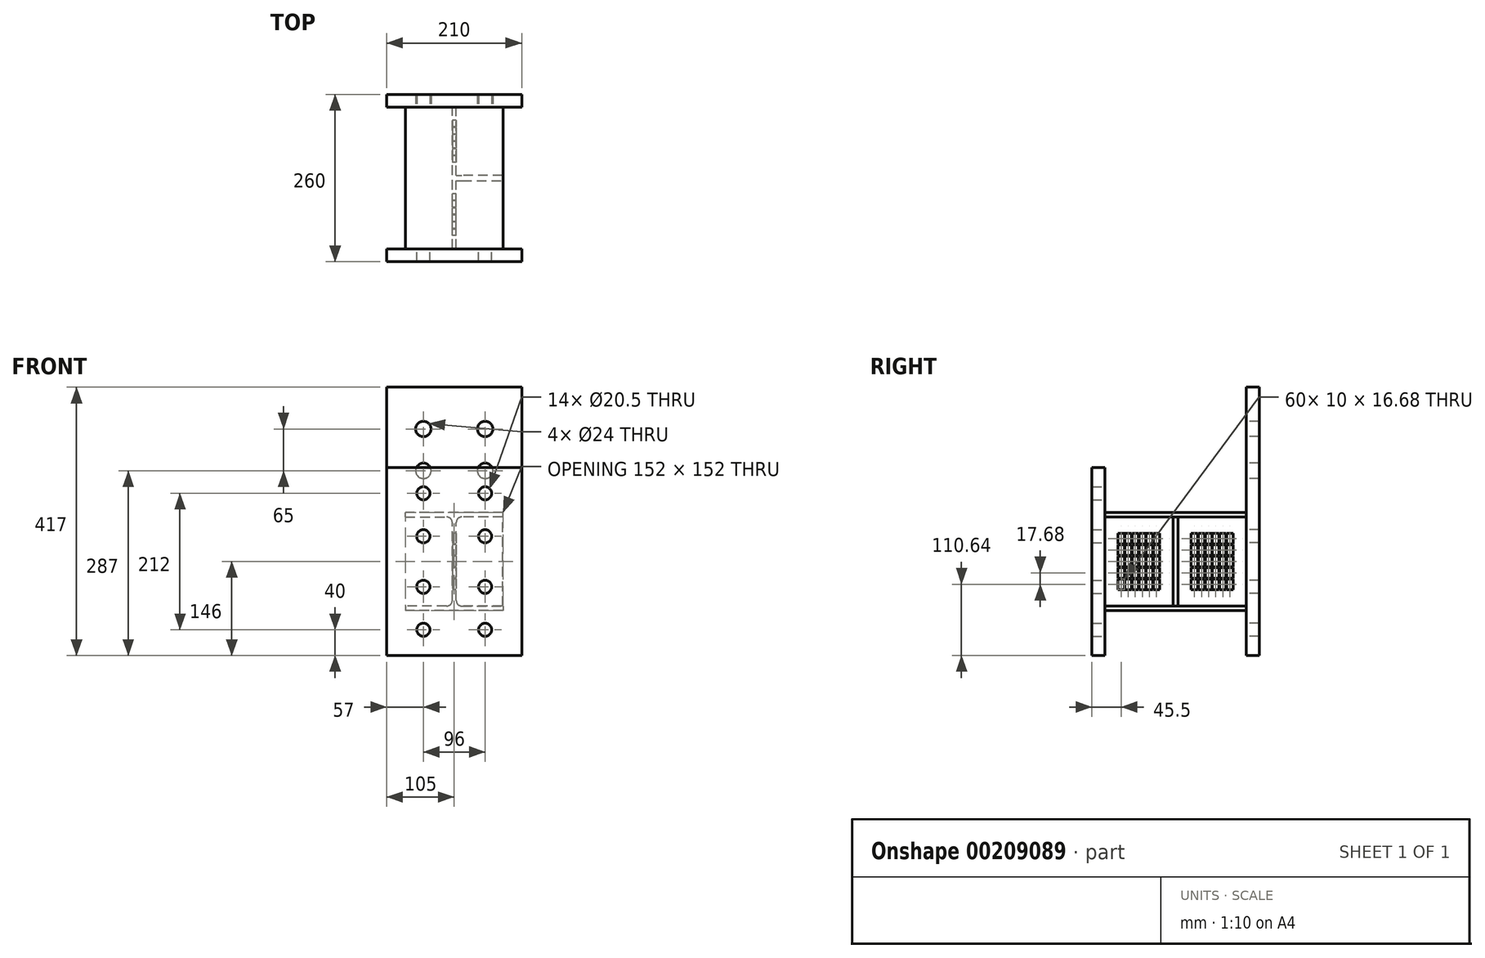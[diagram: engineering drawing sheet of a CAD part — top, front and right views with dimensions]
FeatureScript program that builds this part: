
annotation { "Feature Type Name" : "Feature", "Feature Type Description" : "" }
export const myFeature = defineFeature(function(context is Context, id is Id, definition is map)
    precondition{}
    {
        {
            var Q0;
            Q0=qCreatedBy(makeId("Front.planeOp"),FACE);
            var sketch = newSketch(context, id + "F0", { "sketchPlane" : qUnion([Q0])});
            skLineSegment(sketch, "E0.left", {"start": v(3.05, -60.3) * mm, "end": v(3.05, 60.3) * mm});
            skLineSegment(sketch, "E0.right", {"start": v(-3.05, -60.3) * mm, "end": v(-3.05, 60.3) * mm});
            skPoint(sketch, "E0.middle", {"position": v(0, 0) * mm});
            skLineSegment(sketch, "E1.bottom", {"start": v(76, 69.2) * mm, "end": v(11.95, 69.2) * mm});
            skLineSegment(sketch, "E1.top", {"start": v(76, 76) * mm, "end": v(-76, 76) * mm});
            skLineSegment(sketch, "E1.left", {"start": v(76, 69.2) * mm, "end": v(76, 76) * mm});
            skLineSegment(sketch, "E1.right", {"start": v(-76, 69.2) * mm, "end": v(-76, 76) * mm});
            skLineSegment(sketch, "E2.bottom", {"start": v(-11.95, -69.2) * mm, "end": v(-76, -69.2) * mm});
            skLineSegment(sketch, "E2.top", {"start": v(76, -76) * mm, "end": v(-76, -76) * mm});
            skLineSegment(sketch, "E2.left", {"start": v(76, -69.2) * mm, "end": v(76, -76) * mm});
            skLineSegment(sketch, "E2.right", {"start": v(-76, -69.2) * mm, "end": v(-76, -76) * mm});
            skPoint(sketch, "E3.newPointB", {"position": v(-76, 69.2) * mm});
            skArc(sketch, "E3.filletArc", {"start": v(11.95, 69.2) * mm, "mid": v(5.66, 66.6) * mm, "end": v(3.05, 60.3) * mm});
            skLineSegment(sketch, "E4", {"start": v(-76, 69.2) * mm, "end": v(-11.95, 69.2) * mm});
            skArc(sketch, "E5.filletArc", {"start": v(-3.05, 60.3) * mm, "mid": v(-5.66, 66.6) * mm, "end": v(-11.95, 69.2) * mm});
            skPoint(sketch, "E6.newPointA", {"position": v(76, -69.2) * mm});
            skArc(sketch, "E6.filletArc", {"start": v(-11.95, -69.2) * mm, "mid": v(-5.66, -66.6) * mm, "end": v(-3.05, -60.3) * mm});
            skLineSegment(sketch, "E7", {"start": v(11.95, -69.2) * mm, "end": v(76, -69.2) * mm});
            skArc(sketch, "E8.filletArc", {"start": v(3.05, -60.3) * mm, "mid": v(5.66, -66.6) * mm, "end": v(11.95, -69.2) * mm});
            skSolve(sketch);
        }
        {
            var Q0;
            Q0=qSketchRegion(id+"F0",true);
            extrude(context, id + "F1", {"entities" : qUnion([Q0]), "depth" : 220 * mm, "symmetric" : true});
        }
        {
            var Q0;
            Q0=makeQuery(id+"F1.opExtrude","SWEPT_FACE",FACE,{"disambiguationData":[OSD([sQuery(id+"F0.wireOp",EDGE,"E0.left")])]});
            var sketch = newSketch(context, id + "F2", { "sketchPlane" : qUnion([Q0])});
            skLineSegment(sketch, "E9.bottom", {"start": v(4, -69.2) * mm, "end": v(-4, -69.2) * mm});
            skLineSegment(sketch, "E9.top", {"start": v(4, 69.2) * mm, "end": v(-4, 69.2) * mm});
            skLineSegment(sketch, "E9.left", {"start": v(4, -69.2) * mm, "end": v(4, 69.2) * mm});
            skLineSegment(sketch, "E9.right", {"start": v(-4, -69.2) * mm, "end": v(-4, 69.2) * mm});
            skPoint(sketch, "E9.middle", {"position": v(0, 0) * mm});
            skSolve(sketch);
        }
        {
            var Q0;
            Q0=qSketchRegion(id+"F2",true);
            extrude(context, id + "F3", {"entities" : qUnion([Q0]), "operationType" : NewBodyOperationType.ADD, "depth" : 72 * mm});
        }
        {
            var Q0;
            Q0=makeQuery(id+"F1.opExtrude","CAP_FACE",FACE,{"disambiguationData":[OSD([sQuery(id+"F0.wireOp",EDGE,"E0.left"),sQuery(id+"F0.wireOp",EDGE,"E0.right"),sQuery(id+"F0.wireOp",EDGE,"E1.bottom"),sQuery(id+"F0.wireOp",EDGE,"E1.top"),sQuery(id+"F0.wireOp",EDGE,"E1.left"),sQuery(id+"F0.wireOp",EDGE,"E1.right"),sQuery(id+"F0.wireOp",EDGE,"E2.bottom"),sQuery(id+"F0.wireOp",EDGE,"E2.top"),sQuery(id+"F0.wireOp",EDGE,"E2.left"),sQuery(id+"F0.wireOp",EDGE,"E2.right"),sQuery(id+"F0.wireOp",EDGE,"E3.filletArc"),sQuery(id+"F0.wireOp",EDGE,"E4"),sQuery(id+"F0.wireOp",EDGE,"E5.filletArc"),sQuery(id+"F0.wireOp",EDGE,"E6.filletArc"),sQuery(id+"F0.wireOp",EDGE,"E7"),sQuery(id+"F0.wireOp",EDGE,"E8.filletArc")])],"isStart":false});
            var sketch = newSketch(context, id + "F4", { "sketchPlane" : qUnion([Q0])});
            skLineSegment(sketch, "E10.bottom", {"start": v(105, -146) * mm, "end": v(-105, -146) * mm});
            skLineSegment(sketch, "E10.top", {"start": v(105, 146) * mm, "end": v(-105, 146) * mm});
            skLineSegment(sketch, "E10.left", {"start": v(105, -146) * mm, "end": v(105, 146) * mm});
            skLineSegment(sketch, "E10.right", {"start": v(-105, -146) * mm, "end": v(-105, 146) * mm});
            skPoint(sketch, "E10.middle", {"position": v(0, 0) * mm});
            skCircle(sketch, "E11", {"center": v(-48, 106) * mm, "radius": 10.25 * mm});
            skCircle(sketch, "E12", {"center": v(-48, 39.2) * mm, "radius": 10.25 * mm});
            skCircle(sketch, "E13", {"center": v(-48, -39.2) * mm, "radius": 10.25 * mm});
            skCircle(sketch, "E14", {"center": v(-48, -106) * mm, "radius": 10.25 * mm});
            skCircle(sketch, "E15.MirrorC", {"center": v(48, -39.2) * mm, "radius": 10.25 * mm});
            skCircle(sketch, "E16.MirrorC", {"center": v(48, 39.2) * mm, "radius": 10.25 * mm});
            skCircle(sketch, "E17.MirrorC", {"center": v(48, -106) * mm, "radius": 10.25 * mm});
            skCircle(sketch, "E18.MirrorC", {"center": v(48, 106) * mm, "radius": 10.25 * mm});
            skSolve(sketch);
        }
        {
            var Q0;
            Q0=qSketchRegion(id+"F4",true);
            extrude(context, id + "F5", {"entities" : qUnion([Q0]), "operationType" : NewBodyOperationType.ADD, "depth" : 20 * mm});
        }
        {
            var Q0;
            Q0=makeQuery(id+"F1.opExtrude","CAP_FACE",FACE,{"disambiguationData":[OSD([sQuery(id+"F0.wireOp",EDGE,"E0.left"),sQuery(id+"F0.wireOp",EDGE,"E0.right"),sQuery(id+"F0.wireOp",EDGE,"E1.bottom"),sQuery(id+"F0.wireOp",EDGE,"E1.top"),sQuery(id+"F0.wireOp",EDGE,"E1.left"),sQuery(id+"F0.wireOp",EDGE,"E1.right"),sQuery(id+"F0.wireOp",EDGE,"E2.bottom"),sQuery(id+"F0.wireOp",EDGE,"E2.top"),sQuery(id+"F0.wireOp",EDGE,"E2.left"),sQuery(id+"F0.wireOp",EDGE,"E2.right"),sQuery(id+"F0.wireOp",EDGE,"E3.filletArc"),sQuery(id+"F0.wireOp",EDGE,"E4"),sQuery(id+"F0.wireOp",EDGE,"E5.filletArc"),sQuery(id+"F0.wireOp",EDGE,"E6.filletArc"),sQuery(id+"F0.wireOp",EDGE,"E7"),sQuery(id+"F0.wireOp",EDGE,"E8.filletArc")])],"isStart":true});
            var sketch = newSketch(context, id + "F6", { "sketchPlane" : qUnion([Q0])});
            skLineSegment(sketch, "E19.bottom", {"start": v(-105, -146) * mm, "end": v(105, -146) * mm});
            skLineSegment(sketch, "E19.top", {"start": v(-105, 271) * mm, "end": v(105, 271) * mm});
            skLineSegment(sketch, "E19.left", {"start": v(-105, -146) * mm, "end": v(-105, 271) * mm});
            skLineSegment(sketch, "E19.right", {"start": v(105, 271) * mm, "end": v(105, -146) * mm});
            skCircle(sketch, "E20", {"center": v(-48, 39.2) * mm, "radius": 10.25 * mm});
            skCircle(sketch, "E21.MirrorC", {"center": v(-48, -106) * mm, "radius": 10.25 * mm});
            skCircle(sketch, "E22.MirrorC", {"center": v(-48, -39.2) * mm, "radius": 10.25 * mm});
            skLineSegment(sketch, "E23", {"start": v(0, 0) * mm, "end": v(0, 68.37) * mm});
            skPoint(sketch, "E23.endSnap0", {"position": v(0, 76) * mm});
            skCircle(sketch, "E24.MirrorC", {"center": v(48, -106) * mm, "radius": 10.25 * mm});
            skCircle(sketch, "E25.MirrorC", {"center": v(48, -39.2) * mm, "radius": 10.25 * mm});
            skCircle(sketch, "E26.MirrorC", {"center": v(48, 39.2) * mm, "radius": 10.25 * mm});
            skCircle(sketch, "E27", {"center": v(-48, 141) * mm, "radius": 12 * mm});
            skCircle(sketch, "E28", {"center": v(-48, 206) * mm, "radius": 12 * mm});
            skCircle(sketch, "E29.MirrorC", {"center": v(48, 141) * mm, "radius": 12 * mm});
            skCircle(sketch, "E30.MirrorC", {"center": v(48, 206) * mm, "radius": 12 * mm});
            skSolve(sketch);
        }
        {
            var Q0;
            Q0=qSketchRegion(id+"F6",true);
            extrude(context, id + "F7", {"entities" : qUnion([Q0]), "operationType" : NewBodyOperationType.ADD, "depth" : 20 * mm});
        }
        {
            var Q0;
            {var subQ2=sQuery(id+"F0.wireOp",EDGE,"E0.right");Q0=makeQuery(id+"F3.boolean.opBoolean","SPLIT",FACE,{"disambiguationData":[TD([makeQuery(id+"F3.opExtrude","SWEPT_FACE",FACE,{"disambiguationData":[OSD([sQuery(id+"F2.wireOp",EDGE,"E9.left")])]})])],"derivedFrom":makeQuery(id+"F1.opExtrude","SWEPT_FACE",FACE,{"disambiguationData":[OSD([subQ2])]})});}
            var sketch = newSketch(context, id + "F8", { "sketchPlane" : qUnion([Q0])});
            skPoint(sketch, "E31.middle", {"position": v(0, 0) * mm});
            skPoint(sketch, "E31.middle.positionSnap0", {"position": v(53, 0) * mm});
            skPoint(sketch, "E31.middle.positionSnap1", {"position": v(0, 60.3) * mm});
            skPoint(sketch, "E31.centerSnap0", {"position": v(53, 0) * mm});
            skPoint(sketch, "E31.centerSnap1", {"position": v(0, 60.3) * mm});
            skPoint(sketch, "E32.MirrorP", {"position": v(-35, 0) * mm});
            skPoint(sketch, "E33.middle", {"position": v(-57, 26.52) * mm});
            skPoint(sketch, "E34.middle", {"position": v(-57, 8.84) * mm});
            skPoint(sketch, "E35.middle", {"position": v(-57, -8.84) * mm});
            skPoint(sketch, "E36.middle", {"position": v(-57, -26.52) * mm});
            skPoint(sketch, "E37.middle", {"position": v(-57, -44.2) * mm});
            skPoint(sketch, "E38.middle", {"position": v(-57, 44.2) * mm});
            skPoint(sketch, "E39.middle", {"position": v(-90, 0) * mm});
            skPoint(sketch, "E40.middle", {"position": v(-79, 0) * mm});
            skPoint(sketch, "E41.middle", {"position": v(-68, 0) * mm});
            skPoint(sketch, "E42.middle", {"position": v(-46, 0) * mm});
            skPoint(sketch, "E43.middle", {"position": v(-24, 0) * mm});
            skLineSegment(sketch, "E44.bottom", {"start": v(-89.5, 43.7) * mm, "end": v(-79.5, 43.7) * mm});
            skLineSegment(sketch, "E44.top", {"start": v(-89.5, 27.02) * mm, "end": v(-79.5, 27.02) * mm});
            skLineSegment(sketch, "E44.left", {"start": v(-89.5, 43.7) * mm, "end": v(-89.5, 27.02) * mm});
            skLineSegment(sketch, "E44.right", {"start": v(-79.5, 43.7) * mm, "end": v(-79.5, 27.02) * mm});
            skLineSegment(sketch, "E45.bottom", {"start": v(-78.5, 43.7) * mm, "end": v(-68.5, 43.7) * mm});
            skLineSegment(sketch, "E45.top", {"start": v(-78.5, 27.02) * mm, "end": v(-68.5, 27.02) * mm});
            skLineSegment(sketch, "E45.left", {"start": v(-78.5, 43.7) * mm, "end": v(-78.5, 27.02) * mm});
            skLineSegment(sketch, "E45.right", {"start": v(-68.5, 43.7) * mm, "end": v(-68.5, 27.02) * mm});
            skLineSegment(sketch, "E46.bottom", {"start": v(-67.5, 43.7) * mm, "end": v(-57.5, 43.7) * mm});
            skLineSegment(sketch, "E46.top", {"start": v(-67.5, 27.02) * mm, "end": v(-57.5, 27.02) * mm});
            skLineSegment(sketch, "E46.left", {"start": v(-67.5, 43.7) * mm, "end": v(-67.5, 27.02) * mm});
            skLineSegment(sketch, "E46.right", {"start": v(-57.5, 43.7) * mm, "end": v(-57.5, 27.02) * mm});
            skLineSegment(sketch, "E47.bottom", {"start": v(-56.5, 43.7) * mm, "end": v(-46.5, 43.7) * mm});
            skLineSegment(sketch, "E47.top", {"start": v(-56.5, 27.02) * mm, "end": v(-46.5, 27.02) * mm});
            skLineSegment(sketch, "E47.left", {"start": v(-56.5, 43.7) * mm, "end": v(-56.5, 27.02) * mm});
            skLineSegment(sketch, "E47.right", {"start": v(-46.5, 43.7) * mm, "end": v(-46.5, 27.02) * mm});
            skLineSegment(sketch, "E48.bottom", {"start": v(-45.5, 43.7) * mm, "end": v(-35.5, 43.7) * mm});
            skLineSegment(sketch, "E48.top", {"start": v(-45.5, 27.02) * mm, "end": v(-35.5, 27.02) * mm});
            skLineSegment(sketch, "E48.left", {"start": v(-45.5, 43.7) * mm, "end": v(-45.5, 27.02) * mm});
            skLineSegment(sketch, "E48.right", {"start": v(-35.5, 43.7) * mm, "end": v(-35.5, 27.02) * mm});
            skLineSegment(sketch, "E49.bottom", {"start": v(-34.5, 43.7) * mm, "end": v(-24.5, 43.7) * mm});
            skLineSegment(sketch, "E49.top", {"start": v(-34.5, 27.02) * mm, "end": v(-24.5, 27.02) * mm});
            skLineSegment(sketch, "E49.left", {"start": v(-34.5, 43.7) * mm, "end": v(-34.5, 27.02) * mm});
            skLineSegment(sketch, "E49.right", {"start": v(-24.5, 43.7) * mm, "end": v(-24.5, 27.02) * mm});
            skLineSegment(sketch, "E50.bottom", {"start": v(-89.5, 26.02) * mm, "end": v(-79.5, 26.02) * mm});
            skLineSegment(sketch, "E50.top", {"start": v(-89.5, 9.34) * mm, "end": v(-79.5, 9.34) * mm});
            skLineSegment(sketch, "E50.left", {"start": v(-89.5, 26.02) * mm, "end": v(-89.5, 9.34) * mm});
            skLineSegment(sketch, "E50.right", {"start": v(-79.5, 26.02) * mm, "end": v(-79.5, 9.34) * mm});
            skLineSegment(sketch, "E51.bottom", {"start": v(-78.5, 26.02) * mm, "end": v(-68.5, 26.02) * mm});
            skLineSegment(sketch, "E51.top", {"start": v(-78.5, 9.34) * mm, "end": v(-68.5, 9.34) * mm});
            skLineSegment(sketch, "E51.left", {"start": v(-78.5, 26.02) * mm, "end": v(-78.5, 9.34) * mm});
            skLineSegment(sketch, "E51.right", {"start": v(-68.5, 26.02) * mm, "end": v(-68.5, 9.34) * mm});
            skLineSegment(sketch, "E52.bottom", {"start": v(-67.5, 26.02) * mm, "end": v(-57.5, 26.02) * mm});
            skLineSegment(sketch, "E52.top", {"start": v(-67.5, 9.34) * mm, "end": v(-57.5, 9.34) * mm});
            skLineSegment(sketch, "E52.left", {"start": v(-67.5, 26.02) * mm, "end": v(-67.5, 9.34) * mm});
            skLineSegment(sketch, "E52.right", {"start": v(-57.5, 26.02) * mm, "end": v(-57.5, 9.34) * mm});
            skLineSegment(sketch, "E53.bottom", {"start": v(-56.5, 26.02) * mm, "end": v(-46.5, 26.02) * mm});
            skLineSegment(sketch, "E53.top", {"start": v(-56.5, 9.34) * mm, "end": v(-46.5, 9.34) * mm});
            skLineSegment(sketch, "E53.left", {"start": v(-56.5, 26.02) * mm, "end": v(-56.5, 9.34) * mm});
            skLineSegment(sketch, "E53.right", {"start": v(-46.5, 26.02) * mm, "end": v(-46.5, 9.34) * mm});
            skLineSegment(sketch, "E54.bottom", {"start": v(-45.5, 26.02) * mm, "end": v(-35.5, 26.02) * mm});
            skLineSegment(sketch, "E54.top", {"start": v(-45.5, 9.34) * mm, "end": v(-35.5, 9.34) * mm});
            skLineSegment(sketch, "E54.left", {"start": v(-45.5, 26.02) * mm, "end": v(-45.5, 9.34) * mm});
            skLineSegment(sketch, "E54.right", {"start": v(-35.5, 26.02) * mm, "end": v(-35.5, 9.34) * mm});
            skLineSegment(sketch, "E55.bottom", {"start": v(-34.5, 26.02) * mm, "end": v(-24.5, 26.02) * mm});
            skLineSegment(sketch, "E55.top", {"start": v(-34.5, 9.34) * mm, "end": v(-24.5, 9.34) * mm});
            skLineSegment(sketch, "E55.left", {"start": v(-34.5, 26.02) * mm, "end": v(-34.5, 9.34) * mm});
            skLineSegment(sketch, "E55.right", {"start": v(-24.5, 26.02) * mm, "end": v(-24.5, 9.34) * mm});
            skLineSegment(sketch, "E56.bottom", {"start": v(-89.5, 8.34) * mm, "end": v(-79.5, 8.34) * mm});
            skLineSegment(sketch, "E56.top", {"start": v(-89.5, -8.34) * mm, "end": v(-79.5, -8.34) * mm});
            skLineSegment(sketch, "E56.left", {"start": v(-89.5, 8.34) * mm, "end": v(-89.5, -8.34) * mm});
            skLineSegment(sketch, "E56.right", {"start": v(-79.5, 8.34) * mm, "end": v(-79.5, -8.34) * mm});
            skLineSegment(sketch, "E57.bottom", {"start": v(-78.5, 8.34) * mm, "end": v(-68.5, 8.34) * mm});
            skLineSegment(sketch, "E57.top", {"start": v(-78.5, -8.34) * mm, "end": v(-68.5, -8.34) * mm});
            skLineSegment(sketch, "E57.left", {"start": v(-78.5, 8.34) * mm, "end": v(-78.5, -8.34) * mm});
            skLineSegment(sketch, "E57.right", {"start": v(-68.5, 8.34) * mm, "end": v(-68.5, -8.34) * mm});
            skLineSegment(sketch, "E58.bottom", {"start": v(-67.5, 8.34) * mm, "end": v(-57.5, 8.34) * mm});
            skLineSegment(sketch, "E58.top", {"start": v(-67.5, -8.34) * mm, "end": v(-57.5, -8.34) * mm});
            skLineSegment(sketch, "E58.left", {"start": v(-67.5, 8.34) * mm, "end": v(-67.5, -8.34) * mm});
            skLineSegment(sketch, "E58.right", {"start": v(-57.5, 8.34) * mm, "end": v(-57.5, -8.34) * mm});
            skLineSegment(sketch, "E59.bottom", {"start": v(-56.5, 8.34) * mm, "end": v(-46.5, 8.34) * mm});
            skLineSegment(sketch, "E59.top", {"start": v(-56.5, -8.34) * mm, "end": v(-46.5, -8.34) * mm});
            skLineSegment(sketch, "E59.left", {"start": v(-56.5, 8.34) * mm, "end": v(-56.5, -8.34) * mm});
            skLineSegment(sketch, "E59.right", {"start": v(-46.5, 8.34) * mm, "end": v(-46.5, -8.34) * mm});
            skLineSegment(sketch, "E60.bottom", {"start": v(-45.5, 8.34) * mm, "end": v(-35.5, 8.34) * mm});
            skLineSegment(sketch, "E60.top", {"start": v(-45.5, -8.34) * mm, "end": v(-35.5, -8.34) * mm});
            skLineSegment(sketch, "E60.left", {"start": v(-45.5, 8.34) * mm, "end": v(-45.5, -8.34) * mm});
            skLineSegment(sketch, "E60.right", {"start": v(-35.5, 8.34) * mm, "end": v(-35.5, -8.34) * mm});
            skLineSegment(sketch, "E61.bottom", {"start": v(-34.5, 8.34) * mm, "end": v(-24.5, 8.34) * mm});
            skLineSegment(sketch, "E61.top", {"start": v(-34.5, -8.34) * mm, "end": v(-24.5, -8.34) * mm});
            skLineSegment(sketch, "E61.left", {"start": v(-34.5, 8.34) * mm, "end": v(-34.5, -8.34) * mm});
            skLineSegment(sketch, "E61.right", {"start": v(-24.5, 8.34) * mm, "end": v(-24.5, -8.34) * mm});
            skLineSegment(sketch, "E62.bottom", {"start": v(-89.5, -9.34) * mm, "end": v(-79.5, -9.34) * mm});
            skLineSegment(sketch, "E62.top", {"start": v(-89.5, -26.02) * mm, "end": v(-79.5, -26.02) * mm});
            skLineSegment(sketch, "E62.left", {"start": v(-89.5, -9.34) * mm, "end": v(-89.5, -26.02) * mm});
            skLineSegment(sketch, "E62.right", {"start": v(-79.5, -9.34) * mm, "end": v(-79.5, -26.02) * mm});
            skLineSegment(sketch, "E63.bottom", {"start": v(-78.5, -9.34) * mm, "end": v(-68.5, -9.34) * mm});
            skLineSegment(sketch, "E63.top", {"start": v(-78.5, -26.02) * mm, "end": v(-68.5, -26.02) * mm});
            skLineSegment(sketch, "E63.left", {"start": v(-78.5, -9.34) * mm, "end": v(-78.5, -26.02) * mm});
            skLineSegment(sketch, "E63.right", {"start": v(-68.5, -9.34) * mm, "end": v(-68.5, -26.02) * mm});
            skLineSegment(sketch, "E64.bottom", {"start": v(-67.5, -9.34) * mm, "end": v(-57.5, -9.34) * mm});
            skLineSegment(sketch, "E64.top", {"start": v(-67.5, -26.02) * mm, "end": v(-57.5, -26.02) * mm});
            skLineSegment(sketch, "E64.left", {"start": v(-67.5, -9.34) * mm, "end": v(-67.5, -26.02) * mm});
            skLineSegment(sketch, "E64.right", {"start": v(-57.5, -9.34) * mm, "end": v(-57.5, -26.02) * mm});
            skLineSegment(sketch, "E65.bottom", {"start": v(-56.5, -9.34) * mm, "end": v(-46.5, -9.34) * mm});
            skLineSegment(sketch, "E65.top", {"start": v(-56.5, -26.02) * mm, "end": v(-46.5, -26.02) * mm});
            skLineSegment(sketch, "E65.left", {"start": v(-56.5, -9.34) * mm, "end": v(-56.5, -26.02) * mm});
            skLineSegment(sketch, "E65.right", {"start": v(-46.5, -9.34) * mm, "end": v(-46.5, -26.02) * mm});
            skLineSegment(sketch, "E66.bottom", {"start": v(-45.5, -9.34) * mm, "end": v(-35.5, -9.34) * mm});
            skLineSegment(sketch, "E66.top", {"start": v(-45.5, -26.02) * mm, "end": v(-35.5, -26.02) * mm});
            skLineSegment(sketch, "E66.left", {"start": v(-45.5, -9.34) * mm, "end": v(-45.5, -26.02) * mm});
            skLineSegment(sketch, "E66.right", {"start": v(-35.5, -9.34) * mm, "end": v(-35.5, -26.02) * mm});
            skLineSegment(sketch, "E67.bottom", {"start": v(-34.5, -9.34) * mm, "end": v(-24.5, -9.34) * mm});
            skLineSegment(sketch, "E67.top", {"start": v(-34.5, -26.02) * mm, "end": v(-24.5, -26.02) * mm});
            skLineSegment(sketch, "E67.left", {"start": v(-34.5, -9.34) * mm, "end": v(-34.5, -26.02) * mm});
            skLineSegment(sketch, "E67.right", {"start": v(-24.5, -9.34) * mm, "end": v(-24.5, -26.02) * mm});
            skLineSegment(sketch, "E68.bottom", {"start": v(-89.5, -27.02) * mm, "end": v(-79.5, -27.02) * mm});
            skLineSegment(sketch, "E68.top", {"start": v(-89.5, -43.7) * mm, "end": v(-79.5, -43.7) * mm});
            skLineSegment(sketch, "E68.left", {"start": v(-89.5, -27.02) * mm, "end": v(-89.5, -43.7) * mm});
            skLineSegment(sketch, "E68.right", {"start": v(-79.5, -27.02) * mm, "end": v(-79.5, -43.7) * mm});
            skLineSegment(sketch, "E69.bottom", {"start": v(-78.5, -27.02) * mm, "end": v(-68.5, -27.02) * mm});
            skLineSegment(sketch, "E69.top", {"start": v(-78.5, -43.7) * mm, "end": v(-68.5, -43.7) * mm});
            skLineSegment(sketch, "E69.left", {"start": v(-78.5, -27.02) * mm, "end": v(-78.5, -43.7) * mm});
            skLineSegment(sketch, "E69.right", {"start": v(-68.5, -27.02) * mm, "end": v(-68.5, -43.7) * mm});
            skLineSegment(sketch, "E70.bottom", {"start": v(-67.5, -27.02) * mm, "end": v(-57.5, -27.02) * mm});
            skLineSegment(sketch, "E70.top", {"start": v(-67.5, -43.7) * mm, "end": v(-57.5, -43.7) * mm});
            skLineSegment(sketch, "E70.left", {"start": v(-67.5, -27.02) * mm, "end": v(-67.5, -43.7) * mm});
            skLineSegment(sketch, "E70.right", {"start": v(-57.5, -27.02) * mm, "end": v(-57.5, -43.7) * mm});
            skLineSegment(sketch, "E71.bottom", {"start": v(-56.5, -27.02) * mm, "end": v(-46.5, -27.02) * mm});
            skLineSegment(sketch, "E71.top", {"start": v(-56.5, -43.7) * mm, "end": v(-46.5, -43.7) * mm});
            skLineSegment(sketch, "E71.left", {"start": v(-56.5, -27.02) * mm, "end": v(-56.5, -43.7) * mm});
            skLineSegment(sketch, "E71.right", {"start": v(-46.5, -27.02) * mm, "end": v(-46.5, -43.7) * mm});
            skLineSegment(sketch, "E72.bottom", {"start": v(-45.5, -27.02) * mm, "end": v(-35.5, -27.02) * mm});
            skLineSegment(sketch, "E72.top", {"start": v(-45.5, -43.7) * mm, "end": v(-35.5, -43.7) * mm});
            skLineSegment(sketch, "E72.left", {"start": v(-45.5, -27.02) * mm, "end": v(-45.5, -43.7) * mm});
            skLineSegment(sketch, "E72.right", {"start": v(-35.5, -27.02) * mm, "end": v(-35.5, -43.7) * mm});
            skLineSegment(sketch, "E73.bottom", {"start": v(-34.5, -27.02) * mm, "end": v(-24.5, -27.02) * mm});
            skLineSegment(sketch, "E73.top", {"start": v(-34.5, -43.7) * mm, "end": v(-24.5, -43.7) * mm});
            skLineSegment(sketch, "E73.left", {"start": v(-34.5, -27.02) * mm, "end": v(-34.5, -43.7) * mm});
            skLineSegment(sketch, "E73.right", {"start": v(-24.5, -27.02) * mm, "end": v(-24.5, -43.7) * mm});
            skLineSegment(sketch, "E74", {"start": v(0, 60.3) * mm, "end": v(0, -69) * mm});
            skLineSegment(sketch, "E75.MirrorCS", {"start": v(35.5, 8.34) * mm, "end": v(35.5, -8.34) * mm});
            skLineSegment(sketch, "E76.MirrorCS", {"start": v(79.5, 8.34) * mm, "end": v(79.5, -8.34) * mm});
            skLineSegment(sketch, "E77.MirrorCS", {"start": v(57.5, 8.34) * mm, "end": v(57.5, -8.34) * mm});
            skLineSegment(sketch, "E78.MirrorCS", {"start": v(34.5, 8.34) * mm, "end": v(34.5, -8.34) * mm});
            skLineSegment(sketch, "E79.MirrorCS", {"start": v(67.5, -27.02) * mm, "end": v(57.5, -27.02) * mm});
            skLineSegment(sketch, "E80.MirrorCS", {"start": v(56.5, 8.34) * mm, "end": v(56.5, -8.34) * mm});
            skLineSegment(sketch, "E81.MirrorCS", {"start": v(45.5, 8.34) * mm, "end": v(45.5, -8.34) * mm});
            skLineSegment(sketch, "E82.MirrorCS", {"start": v(89.5, 8.34) * mm, "end": v(89.5, -8.34) * mm});
            skLineSegment(sketch, "E83.MirrorCS", {"start": v(79.5, 43.7) * mm, "end": v(79.5, 27.02) * mm});
            skLineSegment(sketch, "E84.MirrorCS", {"start": v(67.5, 43.7) * mm, "end": v(57.5, 43.7) * mm});
            skLineSegment(sketch, "E85.MirrorCS", {"start": v(67.5, 27.02) * mm, "end": v(57.5, 27.02) * mm});
            skLineSegment(sketch, "E86.MirrorCS", {"start": v(79.5, -27.02) * mm, "end": v(79.5, -43.7) * mm});
            skPoint(sketch, "E87.MirrorP", {"position": v(35, 0) * mm});
            skLineSegment(sketch, "E88.MirrorCS", {"start": v(34.5, -27.02) * mm, "end": v(24.5, -27.02) * mm});
            skLineSegment(sketch, "E89.MirrorCS", {"start": v(78.5, -27.02) * mm, "end": v(68.5, -27.02) * mm});
            skLineSegment(sketch, "E90.MirrorCS", {"start": v(56.5, -26.02) * mm, "end": v(46.5, -26.02) * mm});
            skLineSegment(sketch, "E91.MirrorCS", {"start": v(78.5, 8.34) * mm, "end": v(78.5, -8.34) * mm});
            skLineSegment(sketch, "E92.MirrorCS", {"start": v(24.5, 8.34) * mm, "end": v(24.5, -8.34) * mm});
            skLineSegment(sketch, "E93.MirrorCS", {"start": v(68.5, 8.34) * mm, "end": v(68.5, -8.34) * mm});
            skLineSegment(sketch, "E94.MirrorCS", {"start": v(67.5, 8.34) * mm, "end": v(57.5, 8.34) * mm});
            skLineSegment(sketch, "E95.MirrorCS", {"start": v(89.5, -26.02) * mm, "end": v(79.5, -26.02) * mm});
            skLineSegment(sketch, "E96.MirrorCS", {"start": v(67.5, -8.34) * mm, "end": v(57.5, -8.34) * mm});
            skLineSegment(sketch, "E97.MirrorCS", {"start": v(67.5, -43.7) * mm, "end": v(57.5, -43.7) * mm});
            skLineSegment(sketch, "E98.MirrorCS", {"start": v(45.5, -26.02) * mm, "end": v(35.5, -26.02) * mm});
            skLineSegment(sketch, "E99.MirrorCS", {"start": v(67.5, 8.34) * mm, "end": v(67.5, -8.34) * mm});
            skLineSegment(sketch, "E100.MirrorCS", {"start": v(79.5, -9.34) * mm, "end": v(79.5, -26.02) * mm});
            skLineSegment(sketch, "E101.MirrorCS", {"start": v(79.5, 26.02) * mm, "end": v(79.5, 9.34) * mm});
            skLineSegment(sketch, "E102.MirrorCS", {"start": v(46.5, 8.34) * mm, "end": v(46.5, -8.34) * mm});
            skLineSegment(sketch, "E103.MirrorCS", {"start": v(67.5, 26.02) * mm, "end": v(57.5, 26.02) * mm});
            skLineSegment(sketch, "E104.MirrorCS", {"start": v(67.5, -9.34) * mm, "end": v(57.5, -9.34) * mm});
            skLineSegment(sketch, "E105.MirrorCS", {"start": v(67.5, 9.34) * mm, "end": v(57.5, 9.34) * mm});
            skLineSegment(sketch, "E106.MirrorCS", {"start": v(67.5, -26.02) * mm, "end": v(57.5, -26.02) * mm});
            skLineSegment(sketch, "E107.MirrorCS", {"start": v(67.5, 26.02) * mm, "end": v(67.5, 9.34) * mm});
            skLineSegment(sketch, "E108.MirrorCS", {"start": v(45.5, 43.7) * mm, "end": v(45.5, 27.02) * mm});
            skLineSegment(sketch, "E109.MirrorCS", {"start": v(89.5, -27.02) * mm, "end": v(89.5, -43.7) * mm});
            skLineSegment(sketch, "E110.MirrorCS", {"start": v(67.5, -9.34) * mm, "end": v(67.5, -26.02) * mm});
            skLineSegment(sketch, "E111.MirrorCS", {"start": v(45.5, -27.02) * mm, "end": v(45.5, -43.7) * mm});
            skLineSegment(sketch, "E112.MirrorCS", {"start": v(56.5, 27.02) * mm, "end": v(46.5, 27.02) * mm});
            skLineSegment(sketch, "E113.MirrorCS", {"start": v(56.5, 43.7) * mm, "end": v(56.5, 27.02) * mm});
            skLineSegment(sketch, "E114.MirrorCS", {"start": v(46.5, 43.7) * mm, "end": v(46.5, 27.02) * mm});
            skLineSegment(sketch, "E115.MirrorCS", {"start": v(89.5, 43.7) * mm, "end": v(79.5, 43.7) * mm});
            skLineSegment(sketch, "E116.MirrorCS", {"start": v(89.5, 27.02) * mm, "end": v(79.5, 27.02) * mm});
            skLineSegment(sketch, "E117.MirrorCS", {"start": v(89.5, 43.7) * mm, "end": v(89.5, 27.02) * mm});
            skLineSegment(sketch, "E118.MirrorCS", {"start": v(78.5, 43.7) * mm, "end": v(68.5, 43.7) * mm});
            skLineSegment(sketch, "E119.MirrorCS", {"start": v(78.5, 27.02) * mm, "end": v(68.5, 27.02) * mm});
            skLineSegment(sketch, "E120.MirrorCS", {"start": v(57.5, -9.34) * mm, "end": v(57.5, -26.02) * mm});
            skLineSegment(sketch, "E121.MirrorCS", {"start": v(67.5, 43.7) * mm, "end": v(67.5, 27.02) * mm});
            skLineSegment(sketch, "E122.MirrorCS", {"start": v(35.5, -27.02) * mm, "end": v(35.5, -43.7) * mm});
            skLineSegment(sketch, "E123.MirrorCS", {"start": v(57.5, 43.7) * mm, "end": v(57.5, 27.02) * mm});
            skLineSegment(sketch, "E124.MirrorCS", {"start": v(56.5, 43.7) * mm, "end": v(46.5, 43.7) * mm});
            skLineSegment(sketch, "E125.MirrorCS", {"start": v(57.5, 26.02) * mm, "end": v(57.5, 9.34) * mm});
            skLineSegment(sketch, "E126.MirrorCS", {"start": v(35.5, 43.7) * mm, "end": v(35.5, 27.02) * mm});
            skPoint(sketch, "E127.MirrorP", {"position": v(24, 0) * mm});
            skLineSegment(sketch, "E128.MirrorCS", {"start": v(34.5, 43.7) * mm, "end": v(24.5, 43.7) * mm});
            skLineSegment(sketch, "E129.MirrorCS", {"start": v(56.5, -9.34) * mm, "end": v(46.5, -9.34) * mm});
            skLineSegment(sketch, "E130.MirrorCS", {"start": v(34.5, 8.34) * mm, "end": v(24.5, 8.34) * mm});
            skLineSegment(sketch, "E131.MirrorCS", {"start": v(78.5, 26.02) * mm, "end": v(68.5, 26.02) * mm});
            skPoint(sketch, "E132.MirrorP", {"position": v(46, 0) * mm});
            skLineSegment(sketch, "E133.MirrorCS", {"start": v(78.5, 43.7) * mm, "end": v(78.5, 27.02) * mm});
            skLineSegment(sketch, "E134.MirrorCS", {"start": v(68.5, 43.7) * mm, "end": v(68.5, 27.02) * mm});
            skLineSegment(sketch, "E135.MirrorCS", {"start": v(56.5, 26.02) * mm, "end": v(46.5, 26.02) * mm});
            skLineSegment(sketch, "E136.MirrorCS", {"start": v(78.5, 8.34) * mm, "end": v(68.5, 8.34) * mm});
            skLineSegment(sketch, "E137.MirrorCS", {"start": v(56.5, 9.34) * mm, "end": v(46.5, 9.34) * mm});
            skLineSegment(sketch, "E138.MirrorCS", {"start": v(34.5, 27.02) * mm, "end": v(24.5, 27.02) * mm});
            skLineSegment(sketch, "E139.MirrorCS", {"start": v(78.5, -43.7) * mm, "end": v(68.5, -43.7) * mm});
            skLineSegment(sketch, "E140.MirrorCS", {"start": v(34.5, -8.34) * mm, "end": v(24.5, -8.34) * mm});
            skLineSegment(sketch, "E141.MirrorCS", {"start": v(34.5, -43.7) * mm, "end": v(24.5, -43.7) * mm});
            skLineSegment(sketch, "E142.MirrorCS", {"start": v(78.5, -8.34) * mm, "end": v(68.5, -8.34) * mm});
            skLineSegment(sketch, "E143.MirrorCS", {"start": v(34.5, 43.7) * mm, "end": v(34.5, 27.02) * mm});
            skLineSegment(sketch, "E144.MirrorCS", {"start": v(56.5, 26.02) * mm, "end": v(56.5, 9.34) * mm});
            skLineSegment(sketch, "E145.MirrorCS", {"start": v(78.5, -27.02) * mm, "end": v(78.5, -43.7) * mm});
            skLineSegment(sketch, "E146.MirrorCS", {"start": v(56.5, -9.34) * mm, "end": v(56.5, -26.02) * mm});
            skLineSegment(sketch, "E147.MirrorCS", {"start": v(34.5, -27.02) * mm, "end": v(34.5, -43.7) * mm});
            skLineSegment(sketch, "E148.MirrorCS", {"start": v(46.5, 26.02) * mm, "end": v(46.5, 9.34) * mm});
            skLineSegment(sketch, "E149.MirrorCS", {"start": v(24.5, 43.7) * mm, "end": v(24.5, 27.02) * mm});
            skLineSegment(sketch, "E150.MirrorCS", {"start": v(24.5, -27.02) * mm, "end": v(24.5, -43.7) * mm});
            skLineSegment(sketch, "E151.MirrorCS", {"start": v(68.5, -27.02) * mm, "end": v(68.5, -43.7) * mm});
            skLineSegment(sketch, "E152.MirrorCS", {"start": v(46.5, -9.34) * mm, "end": v(46.5, -26.02) * mm});
            skPoint(sketch, "E153.MirrorP", {"position": v(57, 26.52) * mm});
            skLineSegment(sketch, "E154.MirrorCS", {"start": v(89.5, -9.34) * mm, "end": v(79.5, -9.34) * mm});
            skLineSegment(sketch, "E155.MirrorCS", {"start": v(45.5, 26.02) * mm, "end": v(35.5, 26.02) * mm});
            skLineSegment(sketch, "E156.MirrorCS", {"start": v(89.5, 26.02) * mm, "end": v(79.5, 26.02) * mm});
            skLineSegment(sketch, "E157.MirrorCS", {"start": v(45.5, -9.34) * mm, "end": v(35.5, -9.34) * mm});
            skPoint(sketch, "E158.MirrorP", {"position": v(57, 8.84) * mm});
            skLineSegment(sketch, "E159.MirrorCS", {"start": v(45.5, 9.34) * mm, "end": v(35.5, 9.34) * mm});
            skLineSegment(sketch, "E160.MirrorCS", {"start": v(89.5, 9.34) * mm, "end": v(79.5, 9.34) * mm});
            skPoint(sketch, "E161.MirrorP", {"position": v(57, -8.84) * mm});
            skLineSegment(sketch, "E162.MirrorCS", {"start": v(89.5, -9.34) * mm, "end": v(89.5, -26.02) * mm});
            skLineSegment(sketch, "E163.MirrorCS", {"start": v(45.5, 26.02) * mm, "end": v(45.5, 9.34) * mm});
            skLineSegment(sketch, "E164.MirrorCS", {"start": v(89.5, 26.02) * mm, "end": v(89.5, 9.34) * mm});
            skLineSegment(sketch, "E165.MirrorCS", {"start": v(67.5, -27.02) * mm, "end": v(67.5, -43.7) * mm});
            skLineSegment(sketch, "E166.MirrorCS", {"start": v(45.5, -9.34) * mm, "end": v(45.5, -26.02) * mm});
            skLineSegment(sketch, "E167.MirrorCS", {"start": v(56.5, -43.7) * mm, "end": v(46.5, -43.7) * mm});
            skPoint(sketch, "E168.MirrorP", {"position": v(57, -26.52) * mm});
            skLineSegment(sketch, "E169.MirrorCS", {"start": v(35.5, 26.02) * mm, "end": v(35.5, 9.34) * mm});
            skLineSegment(sketch, "E170.MirrorCS", {"start": v(57.5, -27.02) * mm, "end": v(57.5, -43.7) * mm});
            skLineSegment(sketch, "E171.MirrorCS", {"start": v(35.5, -9.34) * mm, "end": v(35.5, -26.02) * mm});
            skPoint(sketch, "E172.MirrorP", {"position": v(57, 44.2) * mm});
            skLineSegment(sketch, "E173.MirrorCS", {"start": v(78.5, 9.34) * mm, "end": v(68.5, 9.34) * mm});
            skLineSegment(sketch, "E174.MirrorCS", {"start": v(34.5, -26.02) * mm, "end": v(24.5, -26.02) * mm});
            skLineSegment(sketch, "E175.MirrorCS", {"start": v(78.5, -26.02) * mm, "end": v(68.5, -26.02) * mm});
            skLineSegment(sketch, "E176.MirrorCS", {"start": v(56.5, -8.34) * mm, "end": v(46.5, -8.34) * mm});
            skLineSegment(sketch, "E177.MirrorCS", {"start": v(34.5, 9.34) * mm, "end": v(24.5, 9.34) * mm});
            skPoint(sketch, "E178.MirrorP", {"position": v(57, -44.2) * mm});
            skLineSegment(sketch, "E179.MirrorCS", {"start": v(78.5, -9.34) * mm, "end": v(68.5, -9.34) * mm});
            skLineSegment(sketch, "E180.MirrorCS", {"start": v(34.5, 26.02) * mm, "end": v(24.5, 26.02) * mm});
            skLineSegment(sketch, "E181.MirrorCS", {"start": v(56.5, 8.34) * mm, "end": v(46.5, 8.34) * mm});
            skLineSegment(sketch, "E182.MirrorCS", {"start": v(56.5, -27.02) * mm, "end": v(46.5, -27.02) * mm});
            skLineSegment(sketch, "E183.MirrorCS", {"start": v(34.5, -9.34) * mm, "end": v(24.5, -9.34) * mm});
            skPoint(sketch, "E184.MirrorP", {"position": v(90, 0) * mm});
            skLineSegment(sketch, "E185.MirrorCS", {"start": v(78.5, 26.02) * mm, "end": v(78.5, 9.34) * mm});
            skLineSegment(sketch, "E186.MirrorCS", {"start": v(34.5, -9.34) * mm, "end": v(34.5, -26.02) * mm});
            skLineSegment(sketch, "E187.MirrorCS", {"start": v(78.5, -9.34) * mm, "end": v(78.5, -26.02) * mm});
            skLineSegment(sketch, "E188.MirrorCS", {"start": v(34.5, 26.02) * mm, "end": v(34.5, 9.34) * mm});
            skLineSegment(sketch, "E189.MirrorCS", {"start": v(56.5, -27.02) * mm, "end": v(56.5, -43.7) * mm});
            skPoint(sketch, "E190.MirrorP", {"position": v(79, 0) * mm});
            skLineSegment(sketch, "E191.MirrorCS", {"start": v(24.5, -9.34) * mm, "end": v(24.5, -26.02) * mm});
            skLineSegment(sketch, "E192.MirrorCS", {"start": v(68.5, 26.02) * mm, "end": v(68.5, 9.34) * mm});
            skLineSegment(sketch, "E193.MirrorCS", {"start": v(68.5, -9.34) * mm, "end": v(68.5, -26.02) * mm});
            skLineSegment(sketch, "E194.MirrorCS", {"start": v(24.5, 26.02) * mm, "end": v(24.5, 9.34) * mm});
            skLineSegment(sketch, "E195.MirrorCS", {"start": v(46.5, -27.02) * mm, "end": v(46.5, -43.7) * mm});
            skLineSegment(sketch, "E196.MirrorCS", {"start": v(45.5, 43.7) * mm, "end": v(35.5, 43.7) * mm});
            skLineSegment(sketch, "E197.MirrorCS", {"start": v(89.5, -27.02) * mm, "end": v(79.5, -27.02) * mm});
            skLineSegment(sketch, "E198.MirrorCS", {"start": v(89.5, 8.34) * mm, "end": v(79.5, 8.34) * mm});
            skLineSegment(sketch, "E199.MirrorCS", {"start": v(45.5, -27.02) * mm, "end": v(35.5, -27.02) * mm});
            skLineSegment(sketch, "E200.MirrorCS", {"start": v(45.5, 8.34) * mm, "end": v(35.5, 8.34) * mm});
            skPoint(sketch, "E201.MirrorP", {"position": v(68, 0) * mm});
            skLineSegment(sketch, "E202.MirrorCS", {"start": v(45.5, 27.02) * mm, "end": v(35.5, 27.02) * mm});
            skLineSegment(sketch, "E203.MirrorCS", {"start": v(89.5, -43.7) * mm, "end": v(79.5, -43.7) * mm});
            skLineSegment(sketch, "E204.MirrorCS", {"start": v(45.5, -8.34) * mm, "end": v(35.5, -8.34) * mm});
            skLineSegment(sketch, "E205.MirrorCS", {"start": v(45.5, -43.7) * mm, "end": v(35.5, -43.7) * mm});
            skLineSegment(sketch, "E206.MirrorCS", {"start": v(89.5, -8.34) * mm, "end": v(79.5, -8.34) * mm});
            skSolve(sketch);
        }
        {
            var Q0;
            Q0=makeQuery(id+"F8.imprint","IMPRINT",FACE,{"disambiguationData":[TD([[makeQuery(id+"F8.imprint","IMPRINT",EDGE,{"derivedFrom":sQuery(id+"F8.wireOp",EDGE,"E44.bottom")}),-1.0]])]});
            var Q1;
            Q1=makeQuery(id+"F8.imprint","IMPRINT",FACE,{"disambiguationData":[TD([[makeQuery(id+"F8.imprint","IMPRINT",EDGE,{"derivedFrom":sQuery(id+"F8.wireOp",EDGE,"E45.bottom")}),-1.0]])]});
            var Q2;
            Q2=makeQuery(id+"F8.imprint","IMPRINT",FACE,{"disambiguationData":[TD([[makeQuery(id+"F8.imprint","IMPRINT",EDGE,{"derivedFrom":sQuery(id+"F8.wireOp",EDGE,"E46.bottom")}),-1.0]])]});
            var Q3;
            Q3=makeQuery(id+"F8.imprint","IMPRINT",FACE,{"disambiguationData":[TD([[makeQuery(id+"F8.imprint","IMPRINT",EDGE,{"derivedFrom":sQuery(id+"F8.wireOp",EDGE,"E47.bottom")}),-1.0]])]});
            var Q4;
            Q4=makeQuery(id+"F8.imprint","IMPRINT",FACE,{"disambiguationData":[TD([[makeQuery(id+"F8.imprint","IMPRINT",EDGE,{"derivedFrom":sQuery(id+"F8.wireOp",EDGE,"E48.bottom")}),-1.0]])]});
            var Q5;
            Q5=makeQuery(id+"F8.imprint","IMPRINT",FACE,{"disambiguationData":[TD([[makeQuery(id+"F8.imprint","IMPRINT",EDGE,{"derivedFrom":sQuery(id+"F8.wireOp",EDGE,"E49.bottom")}),-1.0]])]});
            var Q6;
            Q6=makeQuery(id+"F8.imprint","IMPRINT",FACE,{"disambiguationData":[TD([[makeQuery(id+"F8.imprint","IMPRINT",EDGE,{"derivedFrom":sQuery(id+"F8.wireOp",EDGE,"E55.bottom")}),-1.0]])]});
            var Q7;
            Q7=makeQuery(id+"F8.imprint","IMPRINT",FACE,{"disambiguationData":[TD([[makeQuery(id+"F8.imprint","IMPRINT",EDGE,{"derivedFrom":sQuery(id+"F8.wireOp",EDGE,"E54.bottom")}),-1.0]])]});
            var Q8;
            Q8=makeQuery(id+"F8.imprint","IMPRINT",FACE,{"disambiguationData":[TD([[makeQuery(id+"F8.imprint","IMPRINT",EDGE,{"derivedFrom":sQuery(id+"F8.wireOp",EDGE,"E53.bottom")}),-1.0]])]});
            var Q9;
            Q9=makeQuery(id+"F8.imprint","IMPRINT",FACE,{"disambiguationData":[TD([[makeQuery(id+"F8.imprint","IMPRINT",EDGE,{"derivedFrom":sQuery(id+"F8.wireOp",EDGE,"E52.bottom")}),-1.0]])]});
            var Q10;
            Q10=makeQuery(id+"F8.imprint","IMPRINT",FACE,{"disambiguationData":[TD([[makeQuery(id+"F8.imprint","IMPRINT",EDGE,{"derivedFrom":sQuery(id+"F8.wireOp",EDGE,"E51.bottom")}),-1.0]])]});
            var Q11;
            Q11=makeQuery(id+"F8.imprint","IMPRINT",FACE,{"disambiguationData":[TD([[makeQuery(id+"F8.imprint","IMPRINT",EDGE,{"derivedFrom":sQuery(id+"F8.wireOp",EDGE,"E50.bottom")}),-1.0]])]});
            var Q12;
            Q12=makeQuery(id+"F8.imprint","IMPRINT",FACE,{"disambiguationData":[TD([[makeQuery(id+"F8.imprint","IMPRINT",EDGE,{"derivedFrom":sQuery(id+"F8.wireOp",EDGE,"E56.bottom")}),-1.0]])]});
            var Q13;
            Q13=makeQuery(id+"F8.imprint","IMPRINT",FACE,{"disambiguationData":[TD([[makeQuery(id+"F8.imprint","IMPRINT",EDGE,{"derivedFrom":sQuery(id+"F8.wireOp",EDGE,"E57.bottom")}),-1.0]])]});
            var Q14;
            Q14=makeQuery(id+"F8.imprint","IMPRINT",FACE,{"disambiguationData":[TD([[makeQuery(id+"F8.imprint","IMPRINT",EDGE,{"derivedFrom":sQuery(id+"F8.wireOp",EDGE,"E58.bottom")}),-1.0]])]});
            var Q15;
            Q15=makeQuery(id+"F8.imprint","IMPRINT",FACE,{"disambiguationData":[TD([[makeQuery(id+"F8.imprint","IMPRINT",EDGE,{"derivedFrom":sQuery(id+"F8.wireOp",EDGE,"E59.bottom")}),-1.0]])]});
            var Q16;
            Q16=makeQuery(id+"F8.imprint","IMPRINT",FACE,{"disambiguationData":[TD([[makeQuery(id+"F8.imprint","IMPRINT",EDGE,{"derivedFrom":sQuery(id+"F8.wireOp",EDGE,"E60.bottom")}),-1.0]])]});
            var Q17;
            Q17=makeQuery(id+"F8.imprint","IMPRINT",FACE,{"disambiguationData":[TD([[makeQuery(id+"F8.imprint","IMPRINT",EDGE,{"derivedFrom":sQuery(id+"F8.wireOp",EDGE,"E61.bottom")}),-1.0]])]});
            var Q18;
            Q18=makeQuery(id+"F8.imprint","IMPRINT",FACE,{"disambiguationData":[TD([[makeQuery(id+"F8.imprint","IMPRINT",EDGE,{"derivedFrom":sQuery(id+"F8.wireOp",EDGE,"E67.bottom")}),-1.0]])]});
            var Q19;
            Q19=makeQuery(id+"F8.imprint","IMPRINT",FACE,{"disambiguationData":[TD([[makeQuery(id+"F8.imprint","IMPRINT",EDGE,{"derivedFrom":sQuery(id+"F8.wireOp",EDGE,"E66.bottom")}),-1.0]])]});
            var Q20;
            Q20=makeQuery(id+"F8.imprint","IMPRINT",FACE,{"disambiguationData":[TD([[makeQuery(id+"F8.imprint","IMPRINT",EDGE,{"derivedFrom":sQuery(id+"F8.wireOp",EDGE,"E65.bottom")}),-1.0]])]});
            var Q21;
            Q21=makeQuery(id+"F8.imprint","IMPRINT",FACE,{"disambiguationData":[TD([[makeQuery(id+"F8.imprint","IMPRINT",EDGE,{"derivedFrom":sQuery(id+"F8.wireOp",EDGE,"E64.bottom")}),-1.0]])]});
            var Q22;
            Q22=makeQuery(id+"F8.imprint","IMPRINT",FACE,{"disambiguationData":[TD([[makeQuery(id+"F8.imprint","IMPRINT",EDGE,{"derivedFrom":sQuery(id+"F8.wireOp",EDGE,"E63.bottom")}),-1.0]])]});
            var Q23;
            Q23=makeQuery(id+"F8.imprint","IMPRINT",FACE,{"disambiguationData":[TD([[makeQuery(id+"F8.imprint","IMPRINT",EDGE,{"derivedFrom":sQuery(id+"F8.wireOp",EDGE,"E62.bottom")}),-1.0]])]});
            var Q24;
            Q24=makeQuery(id+"F8.imprint","IMPRINT",FACE,{"disambiguationData":[TD([[makeQuery(id+"F8.imprint","IMPRINT",EDGE,{"derivedFrom":sQuery(id+"F8.wireOp",EDGE,"E68.bottom")}),-1.0]])]});
            var Q25;
            Q25=makeQuery(id+"F8.imprint","IMPRINT",FACE,{"disambiguationData":[TD([[makeQuery(id+"F8.imprint","IMPRINT",EDGE,{"derivedFrom":sQuery(id+"F8.wireOp",EDGE,"E69.bottom")}),-1.0]])]});
            var Q26;
            Q26=makeQuery(id+"F8.imprint","IMPRINT",FACE,{"disambiguationData":[TD([[makeQuery(id+"F8.imprint","IMPRINT",EDGE,{"derivedFrom":sQuery(id+"F8.wireOp",EDGE,"E70.bottom")}),-1.0]])]});
            var Q27;
            Q27=makeQuery(id+"F8.imprint","IMPRINT",FACE,{"disambiguationData":[TD([[makeQuery(id+"F8.imprint","IMPRINT",EDGE,{"derivedFrom":sQuery(id+"F8.wireOp",EDGE,"E71.bottom")}),-1.0]])]});
            var Q28;
            Q28=makeQuery(id+"F8.imprint","IMPRINT",FACE,{"disambiguationData":[TD([[makeQuery(id+"F8.imprint","IMPRINT",EDGE,{"derivedFrom":sQuery(id+"F8.wireOp",EDGE,"E72.bottom")}),-1.0]])]});
            var Q29;
            Q29=makeQuery(id+"F8.imprint","IMPRINT",FACE,{"disambiguationData":[TD([[makeQuery(id+"F8.imprint","IMPRINT",EDGE,{"derivedFrom":sQuery(id+"F8.wireOp",EDGE,"E73.bottom")}),-1.0]])]});
            var Q30;
            Q30=makeQuery(id+"F8.imprint","IMPRINT",FACE,{"disambiguationData":[TD([[makeQuery(id+"F8.imprint","IMPRINT",EDGE,{"derivedFrom":sQuery(id+"F8.wireOp",EDGE,"E88.MirrorCS")}),1.0]])]});
            var Q31;
            Q31=makeQuery(id+"F8.imprint","IMPRINT",FACE,{"disambiguationData":[TD([[makeQuery(id+"F8.imprint","IMPRINT",EDGE,{"derivedFrom":sQuery(id+"F8.wireOp",EDGE,"E111.MirrorCS")}),-1.0]])]});
            var Q32;
            Q32=makeQuery(id+"F8.imprint","IMPRINT",FACE,{"disambiguationData":[TD([[makeQuery(id+"F8.imprint","IMPRINT",EDGE,{"derivedFrom":sQuery(id+"F8.wireOp",EDGE,"E167.MirrorCS")}),-1.0]])]});
            var Q33;
            Q33=makeQuery(id+"F8.imprint","IMPRINT",FACE,{"disambiguationData":[TD([[makeQuery(id+"F8.imprint","IMPRINT",EDGE,{"derivedFrom":sQuery(id+"F8.wireOp",EDGE,"E79.MirrorCS")}),1.0]])]});
            var Q34;
            Q34=makeQuery(id+"F8.imprint","IMPRINT",FACE,{"disambiguationData":[TD([[makeQuery(id+"F8.imprint","IMPRINT",EDGE,{"derivedFrom":sQuery(id+"F8.wireOp",EDGE,"E89.MirrorCS")}),1.0]])]});
            var Q35;
            Q35=makeQuery(id+"F8.imprint","IMPRINT",FACE,{"disambiguationData":[TD([[makeQuery(id+"F8.imprint","IMPRINT",EDGE,{"derivedFrom":sQuery(id+"F8.wireOp",EDGE,"E86.MirrorCS")}),1.0]])]});
            var Q36;
            Q36=makeQuery(id+"F8.imprint","IMPRINT",FACE,{"disambiguationData":[TD([[makeQuery(id+"F8.imprint","IMPRINT",EDGE,{"derivedFrom":sQuery(id+"F8.wireOp",EDGE,"E95.MirrorCS")}),-1.0]])]});
            var Q37;
            Q37=makeQuery(id+"F8.imprint","IMPRINT",FACE,{"disambiguationData":[TD([[makeQuery(id+"F8.imprint","IMPRINT",EDGE,{"derivedFrom":sQuery(id+"F8.wireOp",EDGE,"E175.MirrorCS")}),-1.0]])]});
            var Q38;
            Q38=makeQuery(id+"F8.imprint","IMPRINT",FACE,{"disambiguationData":[TD([[makeQuery(id+"F8.imprint","IMPRINT",EDGE,{"derivedFrom":sQuery(id+"F8.wireOp",EDGE,"E104.MirrorCS")}),1.0]])]});
            var Q39;
            Q39=makeQuery(id+"F8.imprint","IMPRINT",FACE,{"disambiguationData":[TD([[makeQuery(id+"F8.imprint","IMPRINT",EDGE,{"derivedFrom":sQuery(id+"F8.wireOp",EDGE,"E90.MirrorCS")}),-1.0]])]});
            var Q40;
            Q40=makeQuery(id+"F8.imprint","IMPRINT",FACE,{"disambiguationData":[TD([[makeQuery(id+"F8.imprint","IMPRINT",EDGE,{"derivedFrom":sQuery(id+"F8.wireOp",EDGE,"E98.MirrorCS")}),-1.0]])]});
            var Q41;
            Q41=makeQuery(id+"F8.imprint","IMPRINT",FACE,{"disambiguationData":[TD([[makeQuery(id+"F8.imprint","IMPRINT",EDGE,{"derivedFrom":sQuery(id+"F8.wireOp",EDGE,"E174.MirrorCS")}),-1.0]])]});
            var Q42;
            Q42=makeQuery(id+"F8.imprint","IMPRINT",FACE,{"disambiguationData":[TD([[makeQuery(id+"F8.imprint","IMPRINT",EDGE,{"derivedFrom":sQuery(id+"F8.wireOp",EDGE,"E78.MirrorCS")}),-1.0]])]});
            var Q43;
            Q43=makeQuery(id+"F8.imprint","IMPRINT",FACE,{"disambiguationData":[TD([[makeQuery(id+"F8.imprint","IMPRINT",EDGE,{"derivedFrom":sQuery(id+"F8.wireOp",EDGE,"E75.MirrorCS")}),1.0]])]});
            var Q44;
            Q44=makeQuery(id+"F8.imprint","IMPRINT",FACE,{"disambiguationData":[TD([[makeQuery(id+"F8.imprint","IMPRINT",EDGE,{"derivedFrom":sQuery(id+"F8.wireOp",EDGE,"E80.MirrorCS")}),-1.0]])]});
            var Q45;
            Q45=makeQuery(id+"F8.imprint","IMPRINT",FACE,{"disambiguationData":[TD([[makeQuery(id+"F8.imprint","IMPRINT",EDGE,{"derivedFrom":sQuery(id+"F8.wireOp",EDGE,"E77.MirrorCS")}),1.0]])]});
            var Q46;
            Q46=makeQuery(id+"F8.imprint","IMPRINT",FACE,{"disambiguationData":[TD([[makeQuery(id+"F8.imprint","IMPRINT",EDGE,{"derivedFrom":sQuery(id+"F8.wireOp",EDGE,"E91.MirrorCS")}),-1.0]])]});
            var Q47;
            Q47=makeQuery(id+"F8.imprint","IMPRINT",FACE,{"disambiguationData":[TD([[makeQuery(id+"F8.imprint","IMPRINT",EDGE,{"derivedFrom":sQuery(id+"F8.wireOp",EDGE,"E76.MirrorCS")}),1.0]])]});
            var Q48;
            Q48=makeQuery(id+"F8.imprint","IMPRINT",FACE,{"disambiguationData":[TD([[makeQuery(id+"F8.imprint","IMPRINT",EDGE,{"derivedFrom":sQuery(id+"F8.wireOp",EDGE,"E101.MirrorCS")}),1.0]])]});
            var Q49;
            Q49=makeQuery(id+"F8.imprint","IMPRINT",FACE,{"disambiguationData":[TD([[makeQuery(id+"F8.imprint","IMPRINT",EDGE,{"derivedFrom":sQuery(id+"F8.wireOp",EDGE,"E131.MirrorCS")}),1.0]])]});
            var Q50;
            Q50=makeQuery(id+"F8.imprint","IMPRINT",FACE,{"disambiguationData":[TD([[makeQuery(id+"F8.imprint","IMPRINT",EDGE,{"derivedFrom":sQuery(id+"F8.wireOp",EDGE,"E103.MirrorCS")}),1.0]])]});
            var Q51;
            Q51=makeQuery(id+"F8.imprint","IMPRINT",FACE,{"disambiguationData":[TD([[makeQuery(id+"F8.imprint","IMPRINT",EDGE,{"derivedFrom":sQuery(id+"F8.wireOp",EDGE,"E135.MirrorCS")}),1.0]])]});
            var Q52;
            Q52=makeQuery(id+"F8.imprint","IMPRINT",FACE,{"disambiguationData":[TD([[makeQuery(id+"F8.imprint","IMPRINT",EDGE,{"derivedFrom":sQuery(id+"F8.wireOp",EDGE,"E155.MirrorCS")}),1.0]])]});
            var Q53;
            Q53=makeQuery(id+"F8.imprint","IMPRINT",FACE,{"disambiguationData":[TD([[makeQuery(id+"F8.imprint","IMPRINT",EDGE,{"derivedFrom":sQuery(id+"F8.wireOp",EDGE,"E177.MirrorCS")}),-1.0]])]});
            var Q54;
            Q54=makeQuery(id+"F8.imprint","IMPRINT",FACE,{"disambiguationData":[TD([[makeQuery(id+"F8.imprint","IMPRINT",EDGE,{"derivedFrom":sQuery(id+"F8.wireOp",EDGE,"E108.MirrorCS")}),-1.0]])]});
            var Q55;
            Q55=makeQuery(id+"F8.imprint","IMPRINT",FACE,{"disambiguationData":[TD([[makeQuery(id+"F8.imprint","IMPRINT",EDGE,{"derivedFrom":sQuery(id+"F8.wireOp",EDGE,"E112.MirrorCS")}),-1.0]])]});
            var Q56;
            Q56=makeQuery(id+"F8.imprint","IMPRINT",FACE,{"disambiguationData":[TD([[makeQuery(id+"F8.imprint","IMPRINT",EDGE,{"derivedFrom":sQuery(id+"F8.wireOp",EDGE,"E84.MirrorCS")}),1.0]])]});
            var Q57;
            Q57=makeQuery(id+"F8.imprint","IMPRINT",FACE,{"disambiguationData":[TD([[makeQuery(id+"F8.imprint","IMPRINT",EDGE,{"derivedFrom":sQuery(id+"F8.wireOp",EDGE,"E118.MirrorCS")}),1.0]])]});
            var Q58;
            Q58=makeQuery(id+"F8.imprint","IMPRINT",FACE,{"disambiguationData":[TD([[makeQuery(id+"F8.imprint","IMPRINT",EDGE,{"derivedFrom":sQuery(id+"F8.wireOp",EDGE,"E83.MirrorCS")}),1.0]])]});
            var Q59;
            Q59=makeQuery(id+"F8.imprint","IMPRINT",FACE,{"disambiguationData":[TD([[makeQuery(id+"F8.imprint","IMPRINT",EDGE,{"derivedFrom":sQuery(id+"F8.wireOp",EDGE,"E118.MirrorCS")}),1.0]])]});
            var Q60;
            Q60=makeQuery(id+"F8.imprint","IMPRINT",FACE,{"disambiguationData":[TD([[makeQuery(id+"F8.imprint","IMPRINT",EDGE,{"derivedFrom":sQuery(id+"F8.wireOp",EDGE,"E128.MirrorCS")}),1.0]])]});
            extrude(context, id + "F9", {"entities" : qUnion([Q0, Q1, Q2, Q3, Q4, Q5, Q6, Q7, Q8, Q9, Q10, Q11, Q12, Q13, Q14, Q15, Q16, Q17, Q18, Q19, Q20, Q21, Q22, Q23, Q24, Q25, Q26, Q27, Q28, Q29, Q30, Q31, Q32, Q33, Q34, Q35, Q36, Q37, Q38, Q39, Q40, Q41, Q42, Q43, Q44, Q45, Q46, Q47, Q48, Q49, Q50, Q51, Q52, Q53, Q54, Q55, Q56, Q57, Q58, Q59, Q60]), "operationType" : NewBodyOperationType.REMOVE, "oppositeDirection" : true, "depth" : 6.1 * mm});
        }
    });
